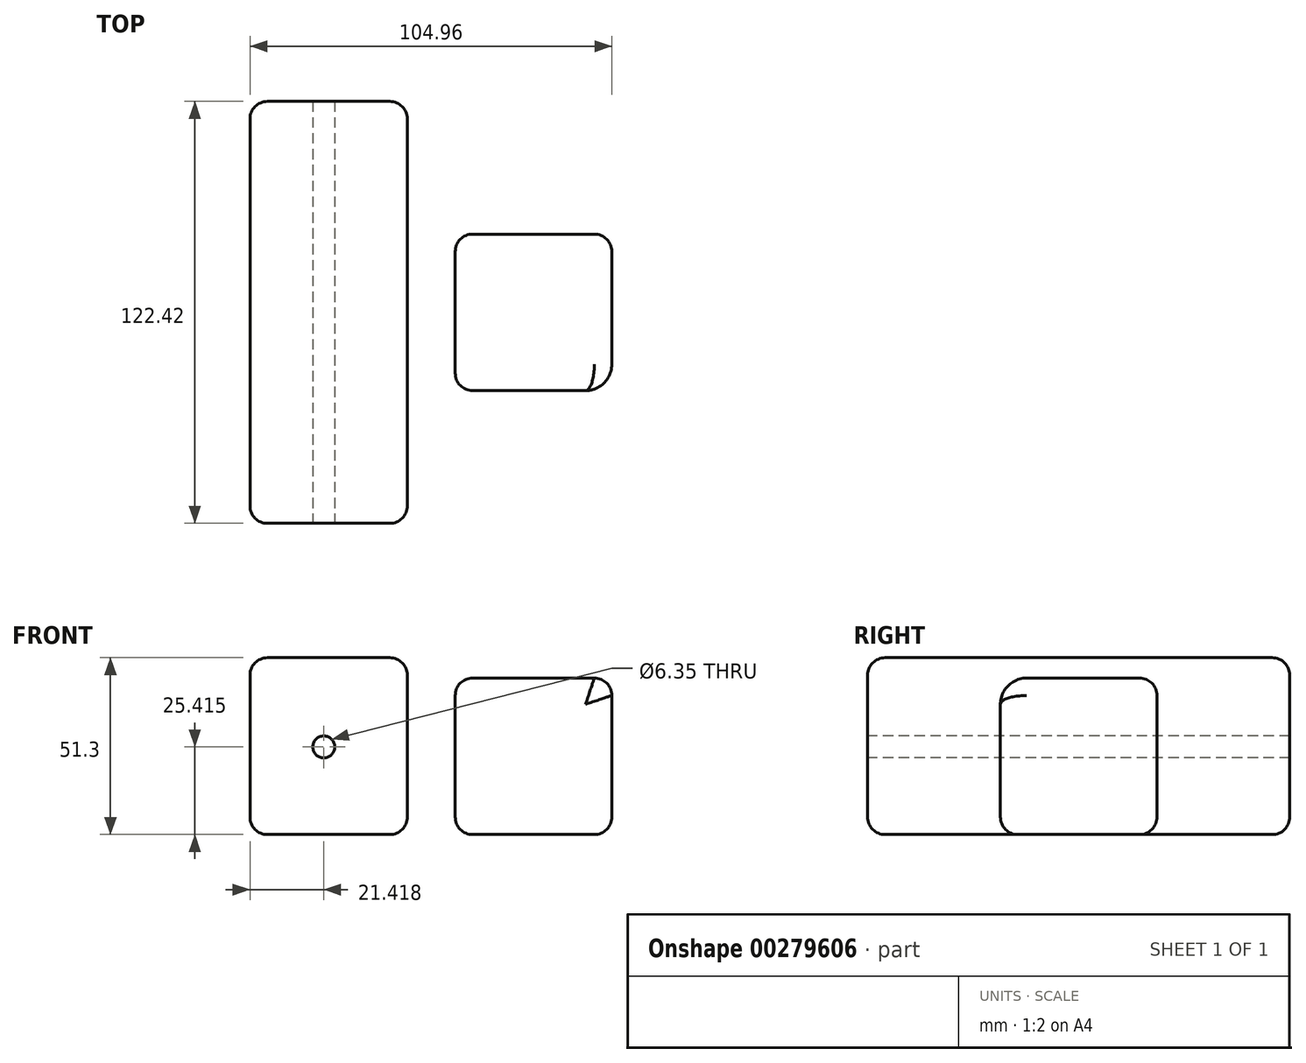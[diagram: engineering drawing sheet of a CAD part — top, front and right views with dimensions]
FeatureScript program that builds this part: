
annotation { "Feature Type Name" : "Feature", "Feature Type Description" : "" }
export const myFeature = defineFeature(function(context is Context, id is Id, definition is map)
    precondition{}
    {
        {
            var Q0;
            Q0=qCreatedBy(makeId("Front.planeOp"),FACE);
            var sketch = newSketch(context, id + "F0", { "sketchPlane" : qUnion([Q0])});
            skLineSegment(sketch, "E0.bottom", {"start": v(0, 0) * mm, "end": v(45.42, 0) * mm});
            skLineSegment(sketch, "E0.top", {"start": v(0, 45.42) * mm, "end": v(45.42, 45.42) * mm});
            skLineSegment(sketch, "E0.left", {"start": v(0, 0) * mm, "end": v(0, 45.42) * mm});
            skLineSegment(sketch, "E0.right", {"start": v(45.42, 0) * mm, "end": v(45.42, 45.42) * mm});
            skSolve(sketch);
        }
        {
            var Q0;
            Q0=makeQuery(id+"F0.imprint","IMPRINT",FACE,{"disambiguationData":[TD([[makeQuery(id+"F0.imprint","IMPRINT",EDGE,{"derivedFrom":sQuery(id+"F0.wireOp",EDGE,"E0.bottom")}),1.0]])]});
            extrude(context, id + "F1", {"entities" : qUnion([Q0]), "endBound" : BoundingType.SYMMETRIC, "depth" : 45.42 * mm});
        }
        {
            var Q0;
            Q0=qCreatedBy(makeId("Front.planeOp"),FACE);
            var sketch = newSketch(context, id + "F2", { "sketchPlane" : qUnion([Q0])});
            skLineSegment(sketch, "E1.bottom", {"start": v(-59.54, 0) * mm, "end": v(-13.88, 0) * mm});
            skLineSegment(sketch, "E1.top", {"start": v(-59.54, 51.3) * mm, "end": v(-13.88, 51.3) * mm});
            skLineSegment(sketch, "E1.left", {"start": v(-59.54, 0) * mm, "end": v(-59.54, 51.3) * mm});
            skLineSegment(sketch, "E1.right", {"start": v(-13.88, 0) * mm, "end": v(-13.88, 51.3) * mm});
            skSolve(sketch);
        }
        {
            var Q0;
            Q0=makeQuery(id+"F2.imprint","IMPRINT",FACE,{"disambiguationData":[TD([[makeQuery(id+"F2.imprint","IMPRINT",EDGE,{"derivedFrom":sQuery(id+"F2.wireOp",EDGE,"E1.bottom")}),1.0]])]});
            extrude(context, id + "F3", {"entities" : qUnion([Q0]), "endBound" : BoundingType.SYMMETRIC, "depth" : 122.43 * mm});
        }
        {
            var Q0;
            Q0=makeQuery(id+"F1.opExtrude","CAP_EDGE",EDGE,{"disambiguationData":[OSD([sQuery(id+"F0.wireOp",EDGE,"E0.right")])],"isStart":false});
            var Q1;
            Q1=makeQuery(id+"F1.opExtrude","CAP_EDGE",EDGE,{"disambiguationData":[OSD([sQuery(id+"F0.wireOp",EDGE,"E0.top")])],"isStart":false});
            fillet(context, id + "F4", {"entities" : qUnion([Q0, Q1]), "radius" : 7.62 * mm, "tangentPropagation" : true, "allowEdgeOverflow" : false});
        }
        {
            var Q0;
            Q0=makeQuery(id+"F1.opExtrude","CAP_EDGE",EDGE,{"disambiguationData":[OSD([sQuery(id+"F0.wireOp",EDGE,"E0.left")])],"isStart":false});
            fillet(context, id + "F5", {"entities" : qUnion([Q0]), "radius" : 5.08 * mm, "tangentPropagation" : true, "allowEdgeOverflow" : false});
        }
        {
            var Q0;
            Q0=makeQuery(id+"F1.opExtrude","CAP_EDGE",EDGE,{"disambiguationData":[OSD([sQuery(id+"F0.wireOp",EDGE,"E0.bottom")])],"isStart":false});
            fillet(context, id + "F6", {"entities" : qUnion([Q0]), "radius" : 5.08 * mm, "tangentPropagation" : true, "allowEdgeOverflow" : false});
        }
        {
            var Q0;
            Q0=makeQuery(id+"F3.opExtrude","CAP_EDGE",EDGE,{"disambiguationData":[OSD([sQuery(id+"F2.wireOp",EDGE,"E1.top")])],"isStart":false});
            fillet(context, id + "F7", {"entities" : qUnion([Q0]), "radius" : 5.08 * mm, "tangentPropagation" : true, "allowEdgeOverflow" : false});
        }
        {
            var Q0;
            Q0=makeQuery(id+"F3.opExtrude","CAP_EDGE",EDGE,{"disambiguationData":[OSD([sQuery(id+"F2.wireOp",EDGE,"E1.right")])],"isStart":false});
            fillet(context, id + "F8", {"entities" : qUnion([Q0]), "radius" : 5.08 * mm, "tangentPropagation" : true, "allowEdgeOverflow" : false});
        }
        {
            var Q0;
            Q0=makeQuery(id+"F3.opExtrude","CAP_EDGE",EDGE,{"disambiguationData":[OSD([sQuery(id+"F2.wireOp",EDGE,"E1.left")])],"isStart":false});
            fillet(context, id + "F9", {"entities" : qUnion([Q0]), "radius" : 5.08 * mm, "tangentPropagation" : true, "allowEdgeOverflow" : false});
        }
        {
            var Q0;
            Q0=makeQuery(id+"F3.opExtrude","CAP_EDGE",EDGE,{"disambiguationData":[OSD([sQuery(id+"F2.wireOp",EDGE,"E1.bottom")])],"isStart":false});
            fillet(context, id + "F10", {"entities" : qUnion([Q0]), "radius" : 5.08 * mm, "tangentPropagation" : true, "allowEdgeOverflow" : false});
        }
        {
            var Q0;
            Q0=makeQuery(id+"F1.opExtrude","CAP_EDGE",EDGE,{"disambiguationData":[OSD([sQuery(id+"F0.wireOp",EDGE,"E0.top")])],"isStart":true});
            fillet(context, id + "F11", {"entities" : qUnion([Q0]), "radius" : 5.08 * mm, "tangentPropagation" : true, "allowEdgeOverflow" : false});
        }
        {
            var Q0;
            Q0=makeQuery(id+"F1.opExtrude","SWEPT_EDGE",EDGE,{"disambiguationData":[OSD([sQuery(id+"F0.wireOp",EDGE,"E0.top"),sQuery(id+"F0.wireOp",EDGE,"E0.right")])]});
            fillet(context, id + "F12", {"entities" : qUnion([Q0]), "radius" : 5.08 * mm, "tangentPropagation" : true, "allowEdgeOverflow" : false});
        }
        {
            var Q0;
            Q0=makeQuery(id+"F3.opExtrude","CAP_EDGE",EDGE,{"disambiguationData":[OSD([sQuery(id+"F2.wireOp",EDGE,"E1.top")])],"isStart":true});
            fillet(context, id + "F13", {"entities" : qUnion([Q0]), "radius" : 5.08 * mm, "tangentPropagation" : true, "allowEdgeOverflow" : false});
        }
        {
            var Q0;
            Q0=makeQuery(id+"F3.opExtrude","CAP_FACE",FACE,{"disambiguationData":[OSD([sQuery(id+"F2.wireOp",EDGE,"E1.bottom"),sQuery(id+"F2.wireOp",EDGE,"E1.top"),sQuery(id+"F2.wireOp",EDGE,"E1.left"),sQuery(id+"F2.wireOp",EDGE,"E1.right")])],"isStart":false});
            var sketch = newSketch(context, id + "F14", { "sketchPlane" : qUnion([Q0])});
            skCircle(sketch, "E2", {"center": v(-38.12, 25.41) * mm, "radius": 6 * mm});
            skSolve(sketch);
        }
        {
            var Q0;
            Q0=sQuery(id+"F14.wireOp",VERTEX,"E2.center");
            var Q1;
            Q1=makeQuery(id+"F3.opExtrude","SWEPT_BODY",BODY,{"disambiguationData":[OSD([sQuery(id+"F2.wireOp",EDGE,"E1.bottom"),sQuery(id+"F2.wireOp",EDGE,"E1.top"),sQuery(id+"F2.wireOp",EDGE,"E1.left"),sQuery(id+"F2.wireOp",EDGE,"E1.right")])]});
            hole(context, id + "F15", {"style" : HoleStyle.SIMPLE, "endStyle" : HoleEndStyle.THROUGH, "holeDiameter" : 6.35 * mm, "tappedDepth" : 12.7 * mm, "tapClearance" : 3, "locations" : qUnion([Q0]), "scope" : qUnion([Q1])});
        }
    });
